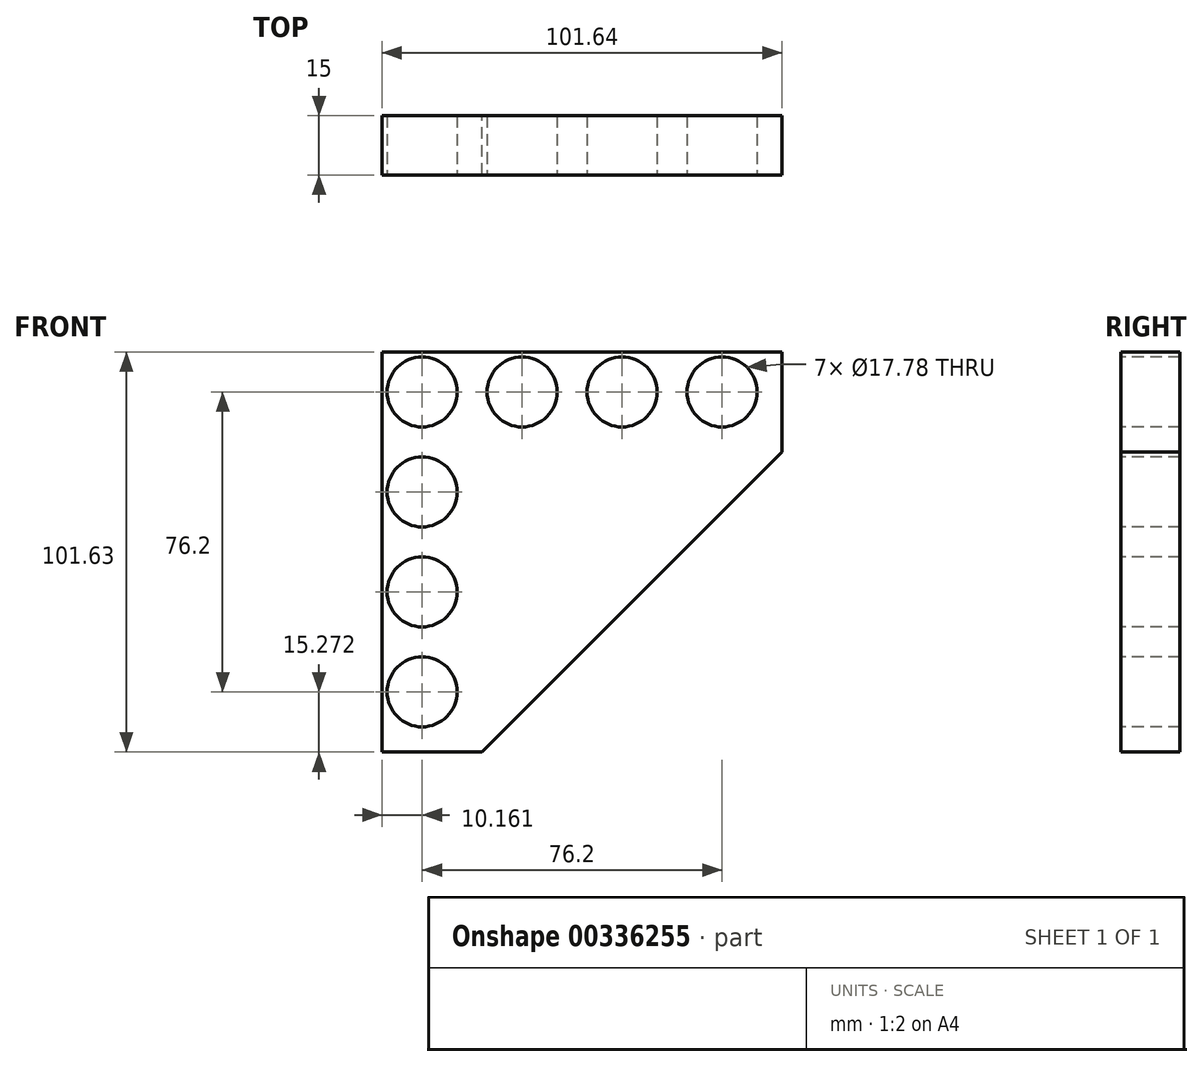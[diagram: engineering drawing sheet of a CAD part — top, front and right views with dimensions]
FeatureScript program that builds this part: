
annotation { "Feature Type Name" : "Feature", "Feature Type Description" : "" }
export const myFeature = defineFeature(function(context is Context, id is Id, definition is map)
    precondition{}
    {
        {
            var Q0;
            Q0=qCreatedBy(makeId("Front.planeOp"),FACE);
            var sketch = newSketch(context, id + "F0", { "sketchPlane" : qUnion([Q0])});
            skLineSegment(sketch, "E0", {"start": v(-43.79, 46.22) * mm, "end": v(57.85, 46.22) * mm});
            skLineSegment(sketch, "E1", {"start": v(57.85, 46.22) * mm, "end": v(57.85, 20.81) * mm});
            skLineSegment(sketch, "E2", {"start": v(-43.79, 46.22) * mm, "end": v(-43.79, -55.41) * mm});
            skLineSegment(sketch, "E3", {"start": v(-43.79, -55.41) * mm, "end": v(-18.38, -55.41) * mm});
            skLineSegment(sketch, "E4", {"start": v(-18.38, -55.41) * mm, "end": v(57.85, 20.81) * mm});
            skSolve(sketch);
        }
        {
            var Q0;
            Q0=makeQuery(id+"F0.imprint","IMPRINT",FACE,{"disambiguationData":[TD([[makeQuery(id+"F0.imprint","IMPRINT",EDGE,{"derivedFrom":sQuery(id+"F0.wireOp",EDGE,"E0")}),-1.0]])]});
            extrude(context, id + "F1", {"entities" : qUnion([Q0]), "depth" : 15 * mm});
        }
        {
            var Q0;
            Q0=makeQuery(id+"F1.opExtrude","CAP_FACE",FACE,{"disambiguationData":[OSD([sQuery(id+"F0.wireOp",EDGE,"E0"),sQuery(id+"F0.wireOp",EDGE,"E1"),sQuery(id+"F0.wireOp",EDGE,"E2"),sQuery(id+"F0.wireOp",EDGE,"E3"),sQuery(id+"F0.wireOp",EDGE,"E4")])],"isStart":false});
            var sketch = newSketch(context, id + "F2", { "sketchPlane" : qUnion([Q0])});
            skCircle(sketch, "E5", {"center": v(-33.63, 36.06) * mm, "radius": 8.9 * mm});
            skCircle(sketch, "E6.0.1.0", {"center": v(-33.63, 10.66) * mm, "radius": 8.9 * mm});
            skCircle(sketch, "E6.0.2.0", {"center": v(-33.63, -14.74) * mm, "radius": 8.9 * mm});
            skCircle(sketch, "E6.0.3.0", {"center": v(-33.63, -40.14) * mm, "radius": 8.9 * mm});
            skLineSegment(sketch, "E6.direction1", {"start": v(-33.63, 36.06) * mm, "end": v(-8.23, 36.06) * mm, "construction": true});
            skLineSegment(sketch, "E6.direction2", {"start": v(-33.63, 36.06) * mm, "end": v(-33.63, 10.66) * mm, "construction": true});
            skCircle(sketch, "E7.1.0.0", {"center": v(-8.23, 36.06) * mm, "radius": 8.9 * mm});
            skCircle(sketch, "E7.2.0.0", {"center": v(17.17, 36.06) * mm, "radius": 8.9 * mm});
            skCircle(sketch, "E7.3.0.0", {"center": v(42.57, 36.06) * mm, "radius": 8.9 * mm});
            skSolve(sketch);
        }
        {
            var Q0;
            Q0 = qSketchRegion(id + "F2", true);
            extrude(context, id + "F3", {"entities" : qUnion([Q0]), "operationType" : NewBodyOperationType.REMOVE, "oppositeDirection" : true, "depth" : 508 * mm});
        }
    });
